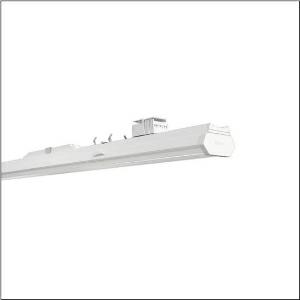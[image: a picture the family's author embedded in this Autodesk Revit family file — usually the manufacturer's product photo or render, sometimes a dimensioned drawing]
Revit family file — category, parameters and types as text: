
# Revit family: licross_r__21_protected_mo_52td12dn4a5g3c_a968
name_source: partatom
category: Lighting Fixtures
units: mm (PartAtom-declared; Revit-internal decimal feet)

## family parameters
Cut with Voids When Loaded = No
Host = Face
Light Source = No
Part Type = Normal
Room Calculation Point = No
Round Connector Dimension = Use Diameter
Shared = No

## types (1)
- --- (1 x LED, 940 lm, 6.8 W, 4000K)
    Apparent Load = 7 VA
    CIE Flux Codes = 73 92 98 99 100
    Color Rendering = 80
    Color Temperature = 4000K
    Default Elevation = 1800 mm
    Description = Licross® 21 Protected MO, luminaire insert, of sheet steel, galvanised, coil coated, white, length: 1.500mm, width: 90mm, height: 103mm, LED rated luminous flux: 10.700lm, light colour: 840, control gear: DALI 2 (for two DALI lines), with plug, 6-pole, with phase selection, for trunking rail, 14-core, mains connection: 220..240V, AC, 50/60Hz, rated input power: 66W, for trunking rail, 14-core, internal wiring halogen-free, for emergency light function, converter,control gear: single battery element, battery: LiFePO4, 9Ah, primary light control with lens, of plastic, primary optical cover: cover, of PMMA, light emission: direct distribution, primary light characteristic: symmetric, protection rating (complete): IP54, insulation class (complete): insulation class I (protective earthing), certification: CE, UKCA, protection symbol: D if used in an environment with non-conductive dust loads with corresponding accessories, impact resistance: IK06, permissible ambient temperature for indoor applications: +5..+35°C, standard: EN 60598-2-22, LABS conformity tested according to VDMA 24364:2018-05, reducing of maximum allowable ambient temperature of 5°C with ceiling mounting, corresponds to IFS (International Featured Standards) requirements for safety and quality in the food industry, packaging unit: 1 piece
    Height = 92 mm
    Lamp = 1 x LED
    Lamp Light Flux = 940 lm
    Lamp Power = 6.8 W
    Lamp count = 1
    Length = 1500 mm
    Luminous efficacy = 138 lm/W
    Manufacturer = Siteco
    ModVariant = No
    Model = 52TD12DN4A5G3C
    Mounting Place = Ceiling
    Mounting Type = Pendant
    Number of Poles = 1
    OnlyDefault = Yes
    Power Factor = 1
    Product Name = Licross® 21 Protected MO
    Product group = luminaire insert | ceiling pendant
    ProductGroupID = 902
    Protection Class = Protection class I
    Protection Degree = IP 54
    RLX_Detail_Level = 1
    RLX_Emergency_Light_Flux = 0 lm
    RLX_Emergency_Type = 0
    RLX_Emergency_Type_DB = No
    RlxData = <blob elided: 24921 chars, md5=e085668a>
    Socket = socket
    Standby Power = 0 W
    System Light Flux = 940 lm
    System Power = 7 W
    Type Comments = : emergency light operation: 3 h
    Type Image = l_1256148.jpg
    URL = http://relux.com
    VarID = @adj_132409
    Voltage = 0 V
    Weight = 0.00 kg
    Width = 88 mm

## geometry (parser evidence)
native form markers: Blend x4, Sweep x9
no freeform markers — native parametric forms only
